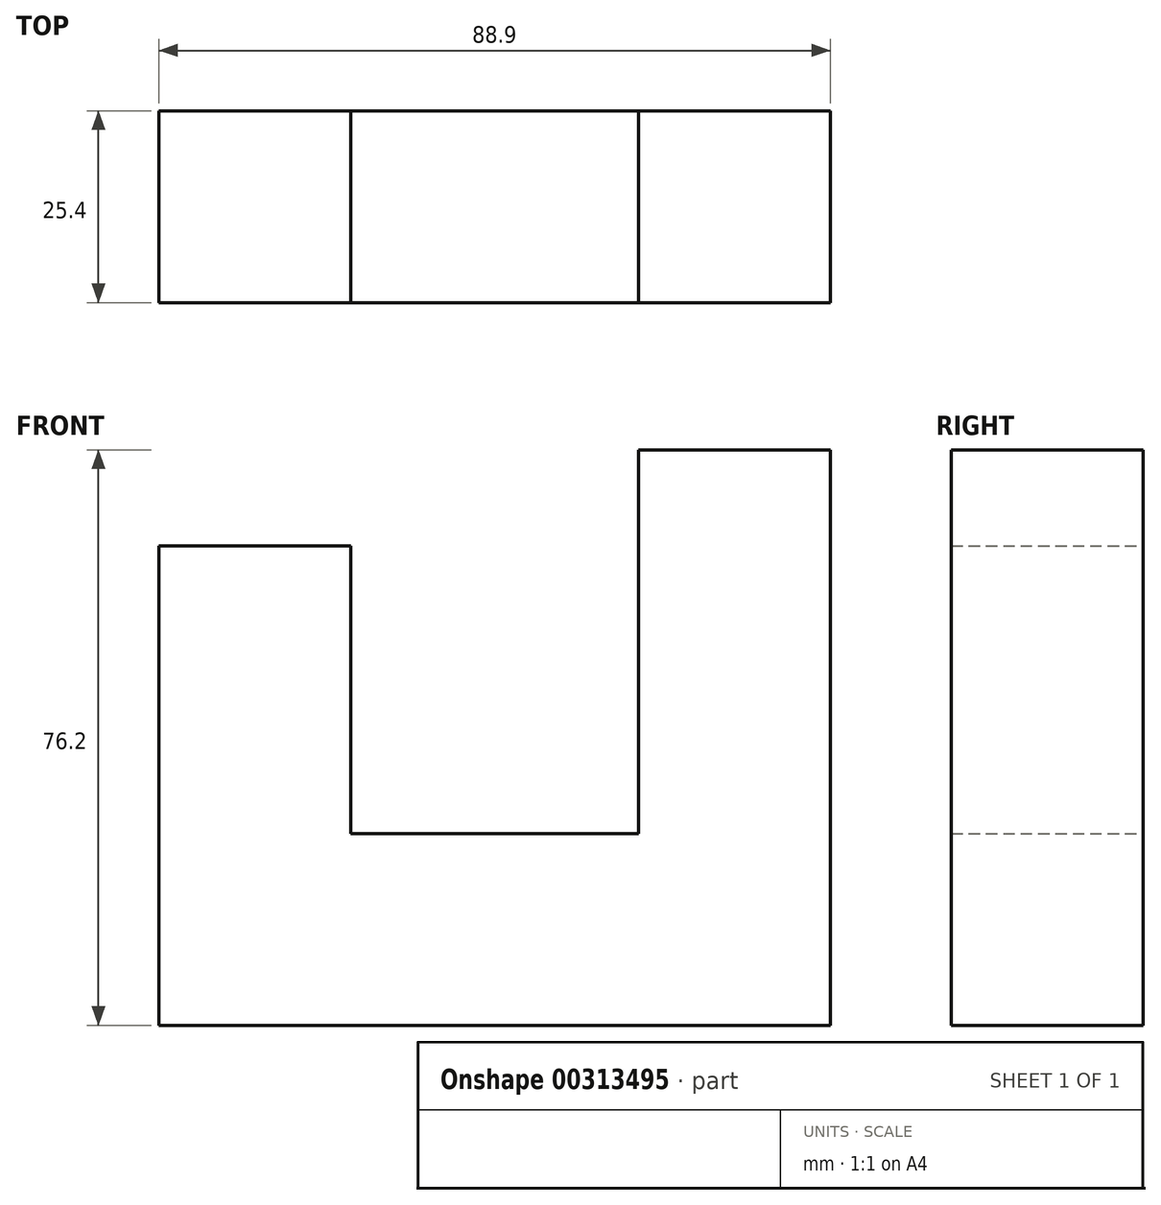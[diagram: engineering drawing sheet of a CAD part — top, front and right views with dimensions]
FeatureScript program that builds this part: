
annotation { "Feature Type Name" : "Feature", "Feature Type Description" : "" }
export const myFeature = defineFeature(function(context is Context, id is Id, definition is map)
    precondition{}
    {
        {
            var Q0;
            Q0=qCreatedBy(makeId("Front.planeOp"),FACE);
            var sketch = newSketch(context, id + "F0", { "sketchPlane" : qUnion([Q0])});
            skLineSegment(sketch, "E0", {"start": v(-72.5, -36.86) * mm, "end": v(16.4, -36.86) * mm});
            skLineSegment(sketch, "E1", {"start": v(-9, -11.46) * mm, "end": v(-47.1, -11.46) * mm});
            skLineSegment(sketch, "E2", {"start": v(16.4, -36.86) * mm, "end": v(16.4, 39.34) * mm});
            skLineSegment(sketch, "E3", {"start": v(16.4, 39.34) * mm, "end": v(-9, 39.34) * mm});
            skLineSegment(sketch, "E4", {"start": v(-9, 39.34) * mm, "end": v(-9, -11.46) * mm});
            skLineSegment(sketch, "E5", {"start": v(-47.1, -11.46) * mm, "end": v(-47.1, 26.64) * mm});
            skLineSegment(sketch, "E6", {"start": v(-47.1, 26.64) * mm, "end": v(-72.5, 26.64) * mm});
            skLineSegment(sketch, "E7", {"start": v(-72.5, 26.64) * mm, "end": v(-72.5, -36.86) * mm});
            skSolve(sketch);
        }
        {
            var Q0;
            Q0=makeQuery(id+"F0.imprint","IMPRINT",FACE,{"disambiguationData":[TD([[makeQuery(id+"F0.imprint","IMPRINT",EDGE,{"derivedFrom":sQuery(id+"F0.wireOp",EDGE,"E0")}),1.0]])]});
            extrude(context, id + "F1", {"entities" : qUnion([Q0]), "depth" : 25.4 * mm});
        }
    });
